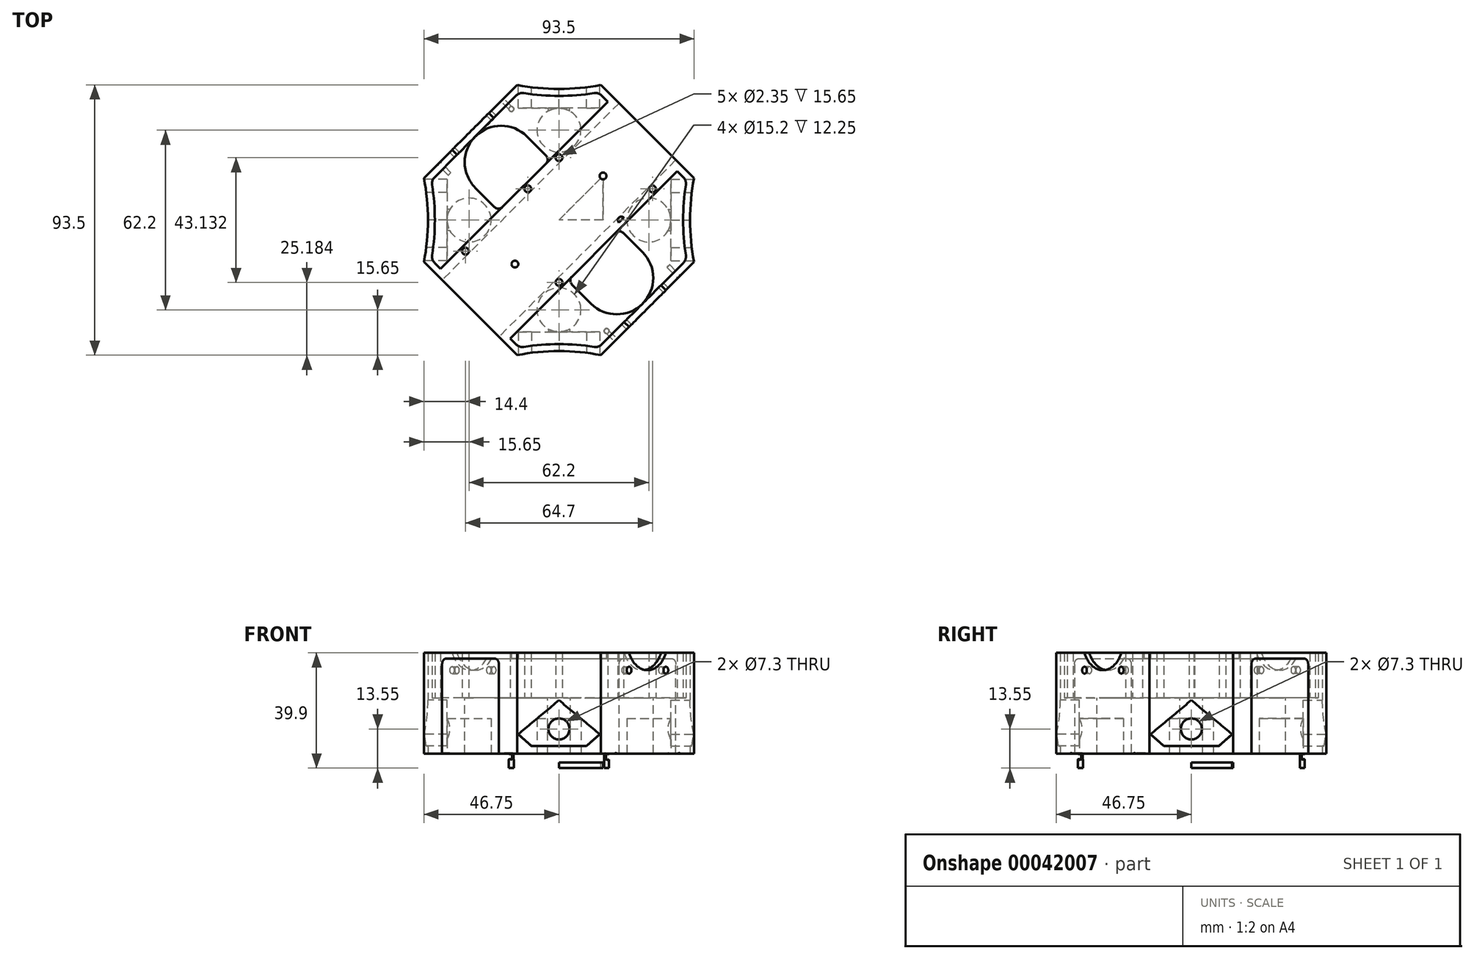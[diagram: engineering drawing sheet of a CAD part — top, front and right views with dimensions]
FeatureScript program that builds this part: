
annotation { "Feature Type Name" : "Feature", "Feature Type Description" : "" }
export const myFeature = defineFeature(function(context is Context, id is Id, definition is map)
    precondition{}
    {
        {
            var Q0;
            Q0=qCreatedBy(makeId("Top.planeOp"),FACE);
            var sketch = newSketch(context, id + "F0", { "sketchPlane" : qUnion([Q0])});
            skLineSegment(sketch, "E0", {"start": v(0, 0) * mm, "end": v(0, 46.75) * mm});
            skLineSegment(sketch, "E1", {"start": v(-14.5, 46.75) * mm, "end": v(14.5, 46.75) * mm});
            skLineSegment(sketch, "E2", {"start": v(0, 0) * mm, "end": v(46.75, 0) * mm});
            skLineSegment(sketch, "E3", {"start": v(46.75, 0) * mm, "end": v(0, 46.75) * mm});
            skLineSegment(sketch, "E4", {"start": v(0, 0) * mm, "end": v(23.37, 23.38) * mm});
            skLineSegment(sketch, "E5", {"start": v(46.75, 14.5) * mm, "end": v(46.75, -14.5) * mm});
            skLineSegment(sketch, "E6", {"start": v(14.5, 46.75) * mm, "end": v(46.75, 14.5) * mm});
            skLineSegment(sketch, "E7.MirrorCS", {"start": v(14.5, -46.75) * mm, "end": v(46.75, -14.5) * mm});
            skLineSegment(sketch, "E8.MirrorCS", {"start": v(46.75, 0) * mm, "end": v(0, -46.75) * mm});
            skLineSegment(sketch, "E9.MirrorCS", {"start": v(0, 0) * mm, "end": v(0, -46.75) * mm});
            skLineSegment(sketch, "E10.MirrorCS", {"start": v(0, 0) * mm, "end": v(23.37, -23.37) * mm});
            skLineSegment(sketch, "E11.MirrorCS", {"start": v(0, 0) * mm, "end": v(-23.37, -23.37) * mm});
            skLineSegment(sketch, "E12.MirrorCS", {"start": v(-46.75, 0) * mm, "end": v(0, -46.75) * mm});
            skLineSegment(sketch, "E13.MirrorCS", {"start": v(0, 0) * mm, "end": v(-23.37, 23.37) * mm});
            skLineSegment(sketch, "E14.MirrorCS", {"start": v(0, 0) * mm, "end": v(-46.75, 0) * mm});
            skLineSegment(sketch, "E15.MirrorCS", {"start": v(-14.5, -46.75) * mm, "end": v(-46.75, -14.5) * mm});
            skLineSegment(sketch, "E16.MirrorCS", {"start": v(-14.5, 46.75) * mm, "end": v(-46.75, 14.5) * mm});
            skLineSegment(sketch, "E17.MirrorCS", {"start": v(-46.75, 0) * mm, "end": v(0, 46.75) * mm});
            skLineSegment(sketch, "E18.MirrorCS", {"start": v(-46.75, 14.5) * mm, "end": v(-46.75, -14.5) * mm});
            skLineSegment(sketch, "E19", {"start": v(-14.5, -46.75) * mm, "end": v(14.5, -46.75) * mm});
            skSolve(sketch);
        }
        {
            var Q0;
            {var subQ1=sQuery(id+"F0.wireOp",EDGE,"E16.MirrorCS");Q0=makeQuery(id+"F0.imprint","IMPRINT",FACE,{"disambiguationData":[TD([[makeQuery(id+"F0.imprint","IMPRINT",EDGE,{"derivedFrom":subQ1}),1.0]])]});}
            var Q1;
            {var subQ0=sQuery(id+"F0.wireOp",EDGE,"E6");Q1=makeQuery(id+"F0.imprint","IMPRINT",FACE,{"disambiguationData":[TD([[makeQuery(id+"F0.imprint","IMPRINT",EDGE,{"derivedFrom":subQ0}),-1.0]])]});}
            var Q2;
            {var subQ1=sQuery(id+"F0.wireOp",EDGE,"E4");Q2=makeQuery(id+"F0.imprint","IMPRINT",FACE,{"disambiguationData":[TD([[makeQuery(id+"F0.imprint","IMPRINT",EDGE,{"derivedFrom":subQ1}),1.0]])]});}
            var Q3;
            {var subQ2=sQuery(id+"F0.wireOp",EDGE,"E0");Q3=makeQuery(id+"F0.imprint","IMPRINT",FACE,{"disambiguationData":[TD([[makeQuery(id+"F0.imprint","IMPRINT",EDGE,{"derivedFrom":subQ2}),1.0]])]});}
            var Q4;
            {var subQ1=sQuery(id+"F0.wireOp",EDGE,"E13.MirrorCS");Q4=makeQuery(id+"F0.imprint","IMPRINT",FACE,{"disambiguationData":[TD([[makeQuery(id+"F0.imprint","IMPRINT",EDGE,{"derivedFrom":subQ1}),1.0]])]});}
            var Q5;
            {var subQ2=sQuery(id+"F0.wireOp",EDGE,"E11.MirrorCS");Q5=makeQuery(id+"F0.imprint","IMPRINT",FACE,{"disambiguationData":[TD([[makeQuery(id+"F0.imprint","IMPRINT",EDGE,{"derivedFrom":subQ2}),-1.0]])]});}
            var Q6;
            {var subQ1=sQuery(id+"F0.wireOp",EDGE,"E15.MirrorCS");Q6=makeQuery(id+"F0.imprint","IMPRINT",FACE,{"disambiguationData":[TD([[makeQuery(id+"F0.imprint","IMPRINT",EDGE,{"derivedFrom":subQ1}),-1.0]])]});}
            var Q7;
            {var subQ2=sQuery(id+"F0.wireOp",EDGE,"E9.MirrorCS");Q7=makeQuery(id+"F0.imprint","IMPRINT",FACE,{"disambiguationData":[TD([[makeQuery(id+"F0.imprint","IMPRINT",EDGE,{"derivedFrom":subQ2}),-1.0]])]});}
            var Q8;
            {var subQ1=sQuery(id+"F0.wireOp",EDGE,"E9.MirrorCS");Q8=makeQuery(id+"F0.imprint","IMPRINT",FACE,{"disambiguationData":[TD([[makeQuery(id+"F0.imprint","IMPRINT",EDGE,{"derivedFrom":subQ1}),1.0]])]});}
            var Q9;
            {var subQ3=sQuery(id+"F0.wireOp",EDGE,"E7.MirrorCS");Q9=makeQuery(id+"F0.imprint","IMPRINT",FACE,{"disambiguationData":[TD([[makeQuery(id+"F0.imprint","IMPRINT",EDGE,{"derivedFrom":subQ3}),1.0]])]});}
            var Q10;
            {var subQ2=sQuery(id+"F0.wireOp",EDGE,"E2");Q10=makeQuery(id+"F0.imprint","IMPRINT",FACE,{"disambiguationData":[TD([[makeQuery(id+"F0.imprint","IMPRINT",EDGE,{"derivedFrom":subQ2}),-1.0]])]});}
            var Q11;
            {var subQ2=sQuery(id+"F0.wireOp",EDGE,"E2");Q11=makeQuery(id+"F0.imprint","IMPRINT",FACE,{"disambiguationData":[TD([[makeQuery(id+"F0.imprint","IMPRINT",EDGE,{"derivedFrom":subQ2}),1.0]])]});}
            extrude(context, id + "F1", {"entities" : qUnion([Q0, Q1, Q2, Q3, Q4, Q5, Q6, Q7, Q8, Q9, Q10, Q11]), "depth" : 24.25 * mm});
        }
        {
            var Q0;
            Q0=makeQuery(id+"F1.opExtrude","SWEPT_FACE",FACE,{"disambiguationData":[OSD([sQuery(id+"F0.wireOp",EDGE,"E19")])]});
            var sketch = newSketch(context, id + "F2", { "sketchPlane" : qUnion([Q0])});
            skLineSegment(sketch, "E20", {"start": v(9.5, 7.65) * mm, "end": v(14.1, 11.7) * mm});
            skLineSegment(sketch, "E21", {"start": v(0, 11.7) * mm, "end": v(0, 7.65) * mm});
            skLineSegment(sketch, "E22.MirrorCS", {"start": v(0, 11.7) * mm, "end": v(-14.1, 11.7) * mm});
            skPoint(sketch, "E23.endSnap0", {"position": v(0, 24.25) * mm});
            skLineSegment(sketch, "E24.MirrorCS", {"start": v(-9.5, 7.65) * mm, "end": v(-14.1, 11.7) * mm});
            skLineSegment(sketch, "E25.MirrorCS", {"start": v(0, 7.65) * mm, "end": v(-9.5, 7.65) * mm});
            skLineSegment(sketch, "E26", {"start": v(-14.1, 11.7) * mm, "end": v(0, 23.5) * mm});
            skLineSegment(sketch, "E27", {"start": v(14.1, 11.7) * mm, "end": v(0, 23.5) * mm});
            skLineSegment(sketch, "E28", {"start": v(0, 11.7) * mm, "end": v(14.1, 11.7) * mm});
            skLineSegment(sketch, "E29", {"start": v(0, 7.65) * mm, "end": v(9.5, 7.65) * mm});
            skLineSegment(sketch, "E30", {"start": v(0, 23.5) * mm, "end": v(0, 11.7) * mm});
            skLineSegment(sketch, "E23", {"start": v(0, 24.25) * mm, "end": v(0, 23.5) * mm});
            skSolve(sketch);
        }
        {
            var Q0;
            Q0 = qSketchRegion(id + "F2", true);
            extrude(context, id + "F3", {"entities" : qUnion([Q0]), "operationType" : NewBodyOperationType.REMOVE, "oppositeDirection" : true, "depth" : 8 * mm});
        }
        {
            var Q0;
            Q0=makeQuery(id+"F1.opExtrude","SWEPT_FACE",FACE,{"disambiguationData":[OSD([sQuery(id+"F0.wireOp",EDGE,"E5")])]});
            var sketch = newSketch(context, id + "F4", { "sketchPlane" : qUnion([Q0])});
            skLineSegment(sketch, "E31", {"start": v(-98.22, 44.38) * mm, "end": v(-93.52, 48.48) * mm});
            skLineSegment(sketch, "E32", {"start": v(-107.72, 48.48) * mm, "end": v(-107.72, 44.38) * mm});
            skLineSegment(sketch, "E33.MirrorCS", {"start": v(-107.72, 48.48) * mm, "end": v(-121.92, 48.48) * mm});
            skPoint(sketch, "E34.endSnap0", {"position": v(-107.72, 61.13) * mm});
            skLineSegment(sketch, "E35.MirrorCS", {"start": v(-117.22, 44.38) * mm, "end": v(-121.92, 48.48) * mm});
            skLineSegment(sketch, "E36.MirrorCS", {"start": v(-107.72, 44.38) * mm, "end": v(-117.22, 44.38) * mm});
            skLineSegment(sketch, "E37", {"start": v(-121.92, 48.48) * mm, "end": v(-107.72, 60.38) * mm});
            skLineSegment(sketch, "E38", {"start": v(-93.52, 48.48) * mm, "end": v(-107.72, 60.38) * mm});
            skLineSegment(sketch, "E39", {"start": v(-107.72, 48.48) * mm, "end": v(-93.52, 48.48) * mm});
            skLineSegment(sketch, "E40", {"start": v(-107.72, 44.38) * mm, "end": v(-98.22, 44.38) * mm});
            skLineSegment(sketch, "E41", {"start": v(-107.72, 60.38) * mm, "end": v(-107.72, 48.48) * mm});
            skLineSegment(sketch, "E34", {"start": v(-107.72, 61.13) * mm, "end": v(-107.72, 60.38) * mm});
            skLineSegment(sketch, "E42", {"start": v(9.5, 7.65) * mm, "end": v(14.1, 11.7) * mm});
            skLineSegment(sketch, "E43", {"start": v(0, 11.7) * mm, "end": v(0, 7.65) * mm});
            skLineSegment(sketch, "E44.MirrorCS", {"start": v(0, 11.7) * mm, "end": v(-14.1, 11.7) * mm});
            skPoint(sketch, "E45.endSnap0", {"position": v(0, 24.25) * mm});
            skLineSegment(sketch, "E46.MirrorCS", {"start": v(-9.5, 7.65) * mm, "end": v(-14.1, 11.7) * mm});
            skLineSegment(sketch, "E47.MirrorCS", {"start": v(0, 7.65) * mm, "end": v(-9.5, 7.65) * mm});
            skLineSegment(sketch, "E48", {"start": v(-14.1, 11.7) * mm, "end": v(0, 23.5) * mm});
            skLineSegment(sketch, "E49", {"start": v(14.1, 11.7) * mm, "end": v(0, 23.5) * mm});
            skLineSegment(sketch, "E50", {"start": v(0, 11.7) * mm, "end": v(14.1, 11.7) * mm});
            skLineSegment(sketch, "E51", {"start": v(0, 7.65) * mm, "end": v(9.5, 7.65) * mm});
            skLineSegment(sketch, "E52", {"start": v(0, 23.5) * mm, "end": v(0, 11.7) * mm});
            skLineSegment(sketch, "E45", {"start": v(0, 24.25) * mm, "end": v(0, 23.5) * mm});
            skSolve(sketch);
        }
        {
            var Q0;
            Q0 = qSketchRegion(id + "F4", true);
            extrude(context, id + "F5", {"entities" : qUnion([Q0]), "operationType" : NewBodyOperationType.REMOVE, "oppositeDirection" : true, "depth" : 8 * mm});
        }
        {
            var Q0;
            Q0=makeQuery(id+"F1.opExtrude","SWEPT_FACE",FACE,{"disambiguationData":[OSD([sQuery(id+"F0.wireOp",EDGE,"E1")])]});
            var sketch = newSketch(context, id + "F6", { "sketchPlane" : qUnion([Q0])});
            skLineSegment(sketch, "E53", {"start": v(9.5, 7.65) * mm, "end": v(14.1, 11.7) * mm});
            skLineSegment(sketch, "E54", {"start": v(0, 11.7) * mm, "end": v(0, 7.65) * mm});
            skLineSegment(sketch, "E55.MirrorCS", {"start": v(0, 11.7) * mm, "end": v(-14.1, 11.7) * mm});
            skPoint(sketch, "E56.endSnap0", {"position": v(0, 24.25) * mm});
            skLineSegment(sketch, "E57.MirrorCS", {"start": v(-9.5, 7.65) * mm, "end": v(-14.1, 11.7) * mm});
            skLineSegment(sketch, "E58.MirrorCS", {"start": v(0, 7.65) * mm, "end": v(-9.5, 7.65) * mm});
            skLineSegment(sketch, "E59", {"start": v(-14.1, 11.7) * mm, "end": v(0, 23.5) * mm});
            skLineSegment(sketch, "E60", {"start": v(14.1, 11.7) * mm, "end": v(0, 23.5) * mm});
            skLineSegment(sketch, "E61", {"start": v(0, 11.7) * mm, "end": v(14.1, 11.7) * mm});
            skLineSegment(sketch, "E62", {"start": v(0, 7.65) * mm, "end": v(9.5, 7.65) * mm});
            skLineSegment(sketch, "E63", {"start": v(0, 23.5) * mm, "end": v(0, 11.7) * mm});
            skLineSegment(sketch, "E56", {"start": v(0, 24.25) * mm, "end": v(0, 23.5) * mm});
            skSolve(sketch);
        }
        {
            var Q0;
            Q0 = qSketchRegion(id + "F6", true);
            extrude(context, id + "F7", {"entities" : qUnion([Q0]), "operationType" : NewBodyOperationType.REMOVE, "oppositeDirection" : true, "depth" : 8 * mm});
        }
        {
            var Q0;
            Q0=makeQuery(id+"F1.opExtrude","SWEPT_FACE",FACE,{"disambiguationData":[OSD([sQuery(id+"F0.wireOp",EDGE,"E18.MirrorCS")])]});
            var sketch = newSketch(context, id + "F8", { "sketchPlane" : qUnion([Q0])});
            skLineSegment(sketch, "E64", {"start": v(9.5, 7.65) * mm, "end": v(14.1, 11.7) * mm});
            skLineSegment(sketch, "E65", {"start": v(0, 11.7) * mm, "end": v(0, 7.65) * mm});
            skLineSegment(sketch, "E66.MirrorCS", {"start": v(0, 11.7) * mm, "end": v(-14.1, 11.7) * mm});
            skPoint(sketch, "E67.endSnap0", {"position": v(0, 24.25) * mm});
            skLineSegment(sketch, "E68.MirrorCS", {"start": v(-9.5, 7.65) * mm, "end": v(-14.1, 11.7) * mm});
            skLineSegment(sketch, "E69.MirrorCS", {"start": v(0, 7.65) * mm, "end": v(-9.5, 7.65) * mm});
            skLineSegment(sketch, "E70", {"start": v(-14.1, 11.7) * mm, "end": v(0, 23.5) * mm});
            skLineSegment(sketch, "E71", {"start": v(14.1, 11.7) * mm, "end": v(0, 23.5) * mm});
            skLineSegment(sketch, "E72", {"start": v(0, 11.7) * mm, "end": v(14.1, 11.7) * mm});
            skLineSegment(sketch, "E73", {"start": v(0, 7.65) * mm, "end": v(9.5, 7.65) * mm});
            skLineSegment(sketch, "E74", {"start": v(0, 23.5) * mm, "end": v(0, 11.7) * mm});
            skLineSegment(sketch, "E67", {"start": v(0, 24.25) * mm, "end": v(0, 23.5) * mm});
            skSolve(sketch);
        }
        {
            var Q0;
            Q0 = qSketchRegion(id + "F8", true);
            extrude(context, id + "F9", {"entities" : qUnion([Q0]), "operationType" : NewBodyOperationType.REMOVE, "oppositeDirection" : true, "depth" : 8 * mm});
        }
        {
            var Q0;
            Q0=qCreatedBy(makeId("Top.planeOp"),FACE);
            var sketch = newSketch(context, id + "F10", { "sketchPlane" : qUnion([Q0])});
            skLineSegment(sketch, "E75", {"start": v(0, 0) * mm, "end": v(0, -121.56) * mm});
            skCircle(sketch, "E76", {"center": v(0, -121.56) * mm, "radius": 76.2 * mm});
            skLineSegment(sketch, "E77.MirrorCS", {"start": v(0, 0) * mm, "end": v(0, 121.56) * mm});
            skCircle(sketch, "E78.MirrorC", {"center": v(0, 121.56) * mm, "radius": 76.2 * mm});
            skLineSegment(sketch, "E79", {"start": v(0, 0) * mm, "end": v(-30.62, -30.63) * mm});
            skCircle(sketch, "E80.MirrorC", {"center": v(-121.56, 0) * mm, "radius": 76.2 * mm});
            skLineSegment(sketch, "E81.MirrorCS", {"start": v(0, 0) * mm, "end": v(121.56, 0) * mm});
            skCircle(sketch, "E82.MirrorC", {"center": v(121.56, 0) * mm, "radius": 76.2 * mm});
            skLineSegment(sketch, "E83.MirrorCS", {"start": v(0, 0) * mm, "end": v(-121.56, 0) * mm});
            skSolve(sketch);
        }
        {
            var Q0;
            Q0 = qSketchRegion(id + "F10", true);
            var Q1;
            {var subQ0=sQuery(id+"F10.wireOp",EDGE,"93edd87a-cf2b-4698-b4c2-4d48644ee807");var subQ3=sQuery(id+"F10.wireOp",EDGE,"E77.MirrorCS");var subQ4=makeQuery(id+"F10.imprint","INTERSECT",VERTEX,{"derivedFrom":[subQ3,subQ0]});Q1=makeQuery(id+"F10.imprint","IMPRINT",FACE,{"disambiguationData":[TD([[makeQuery(id+"F10.imprint","IMPRINT",EDGE,{"disambiguationData":[TD([[subQ4,1.0]])],"derivedFrom":subQ0}),1.0]])]});}
            var Q2;
            {var subQ0=sQuery(id+"F10.wireOp",EDGE,"93edd87a-cf2b-4698-b4c2-4d48644ee807");var subQ3=sQuery(id+"F10.wireOp",EDGE,"E77.MirrorCS");var subQ4=makeQuery(id+"F10.imprint","INTERSECT",VERTEX,{"derivedFrom":[subQ3,subQ0]});Q2=makeQuery(id+"F10.imprint","IMPRINT",FACE,{"disambiguationData":[TD([[makeQuery(id+"F10.imprint","IMPRINT",EDGE,{"disambiguationData":[TD([[subQ4,-1.0]])],"derivedFrom":subQ0}),1.0]])]});}
            var Q3;
            {var subQ0=sQuery(id+"F10.wireOp",EDGE,"93edd87a-cf2b-4698-b4c2-4d48644ee807");var subQ3=sQuery(id+"F10.wireOp",EDGE,"E75");var subQ4=makeQuery(id+"F10.imprint","INTERSECT",VERTEX,{"derivedFrom":[subQ3,subQ0]});Q3=makeQuery(id+"F10.imprint","IMPRINT",FACE,{"disambiguationData":[TD([[makeQuery(id+"F10.imprint","IMPRINT",EDGE,{"disambiguationData":[TD([[subQ4,-1.0]])],"derivedFrom":subQ0}),1.0]])]});}
            var Q4;
            {var subQ0=sQuery(id+"F10.wireOp",EDGE,"E79");var subQ1=sQuery(id+"F10.wireOp",EDGE,"93edd87a-cf2b-4698-b4c2-4d48644ee807");var subQ2=makeQuery(id+"F10.imprint","INTERSECT",VERTEX,{"derivedFrom":[subQ0,subQ1]});Q4=makeQuery(id+"F10.imprint","IMPRINT",FACE,{"disambiguationData":[TD([[makeQuery(id+"F10.imprint","IMPRINT",EDGE,{"disambiguationData":[TD([[subQ2,-1.0]])],"derivedFrom":subQ1}),1.0]])]});}
            var Q5;
            {var subQ0=sQuery(id+"F10.wireOp",EDGE,"93edd87a-cf2b-4698-b4c2-4d48644ee807");var subQ3=sQuery(id+"F10.wireOp",EDGE,"E79");var subQ4=makeQuery(id+"F10.imprint","INTERSECT",VERTEX,{"derivedFrom":[subQ3,subQ0]});Q5=makeQuery(id+"F10.imprint","IMPRINT",FACE,{"disambiguationData":[TD([[makeQuery(id+"F10.imprint","IMPRINT",EDGE,{"disambiguationData":[TD([[subQ4,1.0]])],"derivedFrom":subQ0}),1.0]])]});}
            extrude(context, id + "F11", {"entities" : qUnion([Q0, Q1, Q2, Q3, Q4, Q5]), "operationType" : NewBodyOperationType.REMOVE, "depth" : 45 * mm});
        }
        {
            var Q0;
            Q0=qCreatedBy(makeId("Top.planeOp"),FACE);
            cPlane(context, id + "F12", {"entities" : qUnion([Q0]), "cplaneType" : CPlaneType.OFFSET, "offset" : 5.35 * mm, "width" : 150 * mm, "height" : 150 * mm});
        }
        {
            var Q0;
            Q0=makeQuery(id+"F1.opExtrude","CAP_FACE",FACE,{"disambiguationData":[OSD([sQuery(id+"F0.wireOp",EDGE,"E1"),sQuery(id+"F0.wireOp",EDGE,"E5"),sQuery(id+"F0.wireOp",EDGE,"E6"),sQuery(id+"F0.wireOp",EDGE,"E7.MirrorCS"),sQuery(id+"F0.wireOp",EDGE,"E15.MirrorCS"),sQuery(id+"F0.wireOp",EDGE,"E16.MirrorCS"),sQuery(id+"F0.wireOp",EDGE,"E18.MirrorCS"),sQuery(id+"F0.wireOp",EDGE,"E19")])],"isStart":true});
            var sketch = newSketch(context, id + "F13", { "sketchPlane" : qUnion([Q0])});
            skLineSegment(sketch, "E84", {"start": v(0, 0) * mm, "end": v(23, -23) * mm});
            skLineSegment(sketch, "E85.MirrorCS", {"start": v(0, 0) * mm, "end": v(-23, -23) * mm});
            skCircle(sketch, "E86.MirrorC", {"center": v(0, -31.1) * mm, "radius": 7.6 * mm});
            skCircle(sketch, "E87.MirrorC", {"center": v(-31.1, 0) * mm, "radius": 7.6 * mm});
            skCircle(sketch, "E88.MirrorC", {"center": v(31.1, 0) * mm, "radius": 7.6 * mm});
            skCircle(sketch, "E89", {"center": v(0, 31.1) * mm, "radius": 7.6 * mm});
            skLineSegment(sketch, "E90.MirrorCS", {"start": v(0, 0) * mm, "end": v(-31.1, 0) * mm});
            skLineSegment(sketch, "E91", {"start": v(0, 0) * mm, "end": v(0, 31.1) * mm});
            skLineSegment(sketch, "E92.MirrorCS", {"start": v(0, 0) * mm, "end": v(0, -31.1) * mm});
            skLineSegment(sketch, "E93", {"start": v(0, 0) * mm, "end": v(23, 23) * mm});
            skLineSegment(sketch, "E94.MirrorCS", {"start": v(0, 0) * mm, "end": v(31.1, 0) * mm});
            skSolve(sketch);
        }
        {
            var Q0;
            Q0=qSketchRegion(id+"F13",true);
            extrude(context, id + "F14", {"entities" : qUnion([Q0]), "operationType" : NewBodyOperationType.REMOVE, "oppositeDirection" : true, "depth" : 17.25 * mm});
        }
        {
            var Q0;
            Q0=makeQuery(id+"F1.opExtrude","CAP_FACE",FACE,{"disambiguationData":[OSD([sQuery(id+"F0.wireOp",EDGE,"E1"),sQuery(id+"F0.wireOp",EDGE,"E5"),sQuery(id+"F0.wireOp",EDGE,"E6"),sQuery(id+"F0.wireOp",EDGE,"E7.MirrorCS"),sQuery(id+"F0.wireOp",EDGE,"E15.MirrorCS"),sQuery(id+"F0.wireOp",EDGE,"E16.MirrorCS"),sQuery(id+"F0.wireOp",EDGE,"E18.MirrorCS"),sQuery(id+"F0.wireOp",EDGE,"E19")])],"isStart":false});
            var sketch = newSketch(context, id + "F15", { "sketchPlane" : qUnion([Q0])});
            skLineSegment(sketch, "E95.MirrorCS", {"start": v(0, 0) * mm, "end": v(121.56, 0) * mm});
            skArc(sketch, "E96.MirrorC", {"start": v(46.75, 14.5) * mm, "mid": v(45.36, 0) * mm, "end": v(46.75, -14.5) * mm});
            skArc(sketch, "E97.MirrorC", {"start": v(-46.75, 14.5) * mm, "mid": v(-45.36, 0) * mm, "end": v(-46.75, -14.5) * mm});
            skLineSegment(sketch, "E98", {"start": v(0, 0) * mm, "end": v(0, 121.56) * mm});
            skArc(sketch, "E99", {"start": v(-14.5, 46.75) * mm, "mid": v(0, 45.36) * mm, "end": v(14.5, 46.75) * mm});
            skArc(sketch, "E100.MirrorC", {"start": v(-14.5, -46.75) * mm, "mid": v(0, -45.36) * mm, "end": v(14.5, -46.75) * mm});
            skLineSegment(sketch, "E101", {"start": v(-14.5, 46.75) * mm, "end": v(-14.5, 46.75) * mm});
            skLineSegment(sketch, "E102", {"start": v(14.5, 46.75) * mm, "end": v(46.75, 14.5) * mm});
            skLineSegment(sketch, "E103", {"start": v(46.75, 14.5) * mm, "end": v(46.75, 14.5) * mm});
            skLineSegment(sketch, "E104", {"start": v(46.75, -14.5) * mm, "end": v(14.5, -46.75) * mm});
            skLineSegment(sketch, "E105", {"start": v(14.5, -46.75) * mm, "end": v(14.5, -46.75) * mm});
            skLineSegment(sketch, "E106.trimOffspring", {"start": v(14.5, 46.75) * mm, "end": v(14.5, 46.75) * mm});
            skLineSegment(sketch, "E107.trimOffspring", {"start": v(46.75, -14.5) * mm, "end": v(46.75, -14.5) * mm});
            skLineSegment(sketch, "E108.trimOffspring", {"start": v(-14.5, -46.75) * mm, "end": v(-14.5, -46.75) * mm});
            skLineSegment(sketch, "E109", {"start": v(0, 0) * mm, "end": v(-121.56, 0) * mm});
            skLineSegment(sketch, "E110", {"start": v(-14.5, 46.75) * mm, "end": v(-46.75, 14.5) * mm});
            skLineSegment(sketch, "E111", {"start": v(-46.75, 14.5) * mm, "end": v(-46.75, 14.5) * mm});
            skLineSegment(sketch, "E112", {"start": v(-46.75, -14.5) * mm, "end": v(-14.5, -46.75) * mm});
            skLineSegment(sketch, "E113.trimOffspring", {"start": v(-46.75, -14.5) * mm, "end": v(-46.75, -14.5) * mm});
            skArc(sketch, "E114.0", {"start": v(-12.2, 43.91) * mm, "mid": v(0, 42.96) * mm, "end": v(12.2, 43.91) * mm});
            skLineSegment(sketch, "E114.1", {"start": v(14.79, 43.07) * mm, "end": v(43.07, 14.79) * mm});
            skLineSegment(sketch, "E114.2", {"start": v(-14.79, 43.07) * mm, "end": v(-43.07, 14.79) * mm});
            skArc(sketch, "E114.3", {"start": v(43.91, 12.2) * mm, "mid": v(42.96, 0) * mm, "end": v(43.91, -12.2) * mm});
            skArc(sketch, "E114.4", {"start": v(-43.91, 12.2) * mm, "mid": v(-42.96, 0) * mm, "end": v(-43.91, -12.2) * mm});
            skLineSegment(sketch, "E114.5", {"start": v(-43.07, -14.79) * mm, "end": v(-14.79, -43.07) * mm});
            skArc(sketch, "E114.6", {"start": v(-12.2, -43.91) * mm, "mid": v(0, -42.96) * mm, "end": v(12.2, -43.91) * mm});
            skLineSegment(sketch, "E114.7", {"start": v(43.07, -14.79) * mm, "end": v(14.79, -43.07) * mm});
            skPoint(sketch, "E115.visualSharp", {"position": v(-44.16, -13.7) * mm});
            skArc(sketch, "E115.filletArc", {"start": v(-43.91, -12.2) * mm, "mid": v(-43.8, -13.6) * mm, "end": v(-43.07, -14.79) * mm});
            skPoint(sketch, "E116.visualSharp", {"position": v(-13.7, -44.16) * mm});
            skArc(sketch, "E116.filletArc", {"start": v(-14.79, -43.07) * mm, "mid": v(-13.6, -43.8) * mm, "end": v(-12.2, -43.91) * mm});
            skPoint(sketch, "E117.visualSharp", {"position": v(13.7, -44.16) * mm});
            skArc(sketch, "E117.filletArc", {"start": v(12.2, -43.91) * mm, "mid": v(13.6, -43.8) * mm, "end": v(14.79, -43.07) * mm});
            skPoint(sketch, "E118.visualSharp", {"position": v(44.16, -13.7) * mm});
            skArc(sketch, "E118.filletArc", {"start": v(43.07, -14.79) * mm, "mid": v(43.8, -13.6) * mm, "end": v(43.91, -12.2) * mm});
            skPoint(sketch, "E119.visualSharp", {"position": v(44.16, 13.7) * mm});
            skArc(sketch, "E119.filletArc", {"start": v(43.91, 12.2) * mm, "mid": v(43.8, 13.6) * mm, "end": v(43.07, 14.79) * mm});
            skPoint(sketch, "E120.visualSharp", {"position": v(13.7, 44.16) * mm});
            skArc(sketch, "E120.filletArc", {"start": v(14.79, 43.07) * mm, "mid": v(13.6, 43.8) * mm, "end": v(12.2, 43.91) * mm});
            skPoint(sketch, "E121.visualSharp", {"position": v(-44.16, 13.7) * mm});
            skArc(sketch, "E121.filletArc", {"start": v(-43.07, 14.79) * mm, "mid": v(-43.8, 13.6) * mm, "end": v(-43.91, 12.2) * mm});
            skPoint(sketch, "E122.visualSharp", {"position": v(-13.7, 44.16) * mm});
            skArc(sketch, "E122.filletArc", {"start": v(-12.2, 43.91) * mm, "mid": v(-13.6, 43.8) * mm, "end": v(-14.79, 43.07) * mm});
            skSolve(sketch);
        }
        {
            var Q0;
            Q0=makeQuery(id+"F15.imprint","IMPRINT",FACE,{"disambiguationData":[TD([[makeQuery(id+"F15.imprint","IMPRINT",EDGE,{"derivedFrom":sQuery(id+"F15.wireOp",EDGE,"38fca557-5818-491b-96ee-555abbfffb0f.0")}),1.0]])]});
            var Q1;
            Q1=makeQuery(id+"F15.imprint","IMPRINT",FACE,{"disambiguationData":[TD([[makeQuery(id+"F15.imprint","IMPRINT",EDGE,{"derivedFrom":sQuery(id+"F15.wireOp",EDGE,"38fca557-5818-491b-96ee-555abbfffb0f.1")}),1.0]])]});
            var Q2;
            Q2=makeQuery(id+"F15.imprint","IMPRINT",FACE,{"disambiguationData":[TD([[makeQuery(id+"F15.imprint","IMPRINT",EDGE,{"derivedFrom":sQuery(id+"F15.wireOp",EDGE,"d639dd6d-9a94-4636-acb7-059c743e6398.0")}),-1.0]])]});
            var Q3;
            Q3=makeQuery(id+"F15.imprint","IMPRINT",FACE,{"disambiguationData":[TD([[makeQuery(id+"F15.imprint","IMPRINT",EDGE,{"derivedFrom":sQuery(id+"F15.wireOp",EDGE,"d639dd6d-9a94-4636-acb7-059c743e6398.1")}),-1.0]])]});
            var Q4;
            {var subQ4=sQuery(id+"F15.wireOp",EDGE,"E102");Q4=makeQuery(id+"F15.imprint","IMPRINT",FACE,{"disambiguationData":[TD([[makeQuery(id+"F15.imprint","IMPRINT",EDGE,{"derivedFrom":subQ4}),-1.0]])]});}
            var Q5;
            {var subQ7=sQuery(id+"F15.wireOp",EDGE,"E114.2");Q5=makeQuery(id+"F15.imprint","IMPRINT",FACE,{"disambiguationData":[TD([[makeQuery(id+"F15.imprint","IMPRINT",EDGE,{"derivedFrom":subQ7}),-1.0]])]});}
            var Q6;
            {var subQ0=sQuery(id+"F15.wireOp",EDGE,"E104");Q6=makeQuery(id+"F15.imprint","IMPRINT",FACE,{"disambiguationData":[TD([[makeQuery(id+"F15.imprint","IMPRINT",EDGE,{"derivedFrom":subQ0}),1.0]])]});}
            var Q7;
            {var subQ1=sQuery(id+"F0.wireOp",EDGE,"E16.MirrorCS");var subQ3=makeQuery(id+"F1.opExtrude","CAP_EDGE",EDGE,{"disambiguationData":[OSD([subQ1])],"isStart":false});Q7=makeQuery(id+"F15.imprint","IMPRINT",FACE,{"disambiguationData":[TD([[makeQuery(id+"F15.imprint","IMPRINT",EDGE,{"derivedFrom":subQ3}),1.0]])]});}
            var Q8;
            {var subQ1=sQuery(id+"F0.wireOp",EDGE,"E15.MirrorCS");var subQ3=makeQuery(id+"F1.opExtrude","CAP_EDGE",EDGE,{"disambiguationData":[OSD([subQ1])],"isStart":false});Q8=makeQuery(id+"F15.imprint","IMPRINT",FACE,{"disambiguationData":[TD([[makeQuery(id+"F15.imprint","IMPRINT",EDGE,{"derivedFrom":subQ3}),-1.0]])]});}
            extrude(context, id + "F16", {"entities" : qUnion([Q0, Q1, Q2, Q3, Q4, Q5, Q6, Q7, Q8]), "operationType" : NewBodyOperationType.ADD, "depth" : 15.65 * mm});
        }
        {
            var Q0;
            Q0=makeQuery(id+"F3.boolean.opBoolean","COPY",FACE,{"derivedFrom":makeQuery(id+"F3.opExtrude","CAP_FACE",FACE,{"disambiguationData":[OSD([sQuery(id+"F2.wireOp",EDGE,"E20"),sQuery(id+"F2.wireOp",EDGE,"E24.MirrorCS"),sQuery(id+"F2.wireOp",EDGE,"E25.MirrorCS"),sQuery(id+"F2.wireOp",EDGE,"E26"),sQuery(id+"F2.wireOp",EDGE,"E27"),sQuery(id+"F2.wireOp",EDGE,"E29")])],"isStart":false})});
            var sketch = newSketch(context, id + "F17", { "sketchPlane" : qUnion([Q0])});
            skLineSegment(sketch, "E123", {"start": v(0, 13.55) * mm, "end": v(0, 7.65) * mm});
            skCircle(sketch, "E124", {"center": v(0, 13.55) * mm, "radius": 3.65 * mm});
            skSolve(sketch);
        }
        {
            var Q0;
            Q0 = qSketchRegion(id + "F17", true);
            extrude(context, id + "F18", {"entities" : qUnion([Q0]), "operationType" : NewBodyOperationType.REMOVE, "oppositeDirection" : true, "depth" : 5 * mm});
        }
        {
            var Q0;
            Q0=makeQuery(id+"F5.boolean.opBoolean","COPY",FACE,{"derivedFrom":makeQuery(id+"F5.opExtrude","CAP_FACE",FACE,{"disambiguationData":[OSD([sQuery(id+"F4.wireOp",EDGE,"E42"),sQuery(id+"F4.wireOp",EDGE,"E46.MirrorCS"),sQuery(id+"F4.wireOp",EDGE,"E47.MirrorCS"),sQuery(id+"F4.wireOp",EDGE,"E48"),sQuery(id+"F4.wireOp",EDGE,"E49"),sQuery(id+"F4.wireOp",EDGE,"E51")])],"isStart":false})});
            var sketch = newSketch(context, id + "F19", { "sketchPlane" : qUnion([Q0])});
            skLineSegment(sketch, "E125", {"start": v(0, 13.55) * mm, "end": v(0, 7.65) * mm});
            skCircle(sketch, "E126", {"center": v(0, 13.55) * mm, "radius": 3.65 * mm});
            skSolve(sketch);
        }
        {
            var Q0;
            Q0 = qSketchRegion(id + "F19", true);
            extrude(context, id + "F20", {"entities" : qUnion([Q0]), "operationType" : NewBodyOperationType.REMOVE, "oppositeDirection" : true, "depth" : 5 * mm});
        }
        {
            var Q0;
            Q0=makeQuery(id+"F7.boolean.opBoolean","COPY",FACE,{"derivedFrom":makeQuery(id+"F7.opExtrude","CAP_FACE",FACE,{"disambiguationData":[OSD([sQuery(id+"F6.wireOp",EDGE,"E53"),sQuery(id+"F6.wireOp",EDGE,"E57.MirrorCS"),sQuery(id+"F6.wireOp",EDGE,"E58.MirrorCS"),sQuery(id+"F6.wireOp",EDGE,"E59"),sQuery(id+"F6.wireOp",EDGE,"E60"),sQuery(id+"F6.wireOp",EDGE,"E62")])],"isStart":false})});
            var sketch = newSketch(context, id + "F21", { "sketchPlane" : qUnion([Q0])});
            skLineSegment(sketch, "E127", {"start": v(0, 13.55) * mm, "end": v(0, 7.65) * mm});
            skCircle(sketch, "E128", {"center": v(0, 13.55) * mm, "radius": 3.65 * mm});
            skSolve(sketch);
        }
        {
            var Q0;
            Q0=makeQuery(id+"F9.boolean.opBoolean","COPY",FACE,{"derivedFrom":makeQuery(id+"F9.opExtrude","CAP_FACE",FACE,{"disambiguationData":[OSD([sQuery(id+"F8.wireOp",EDGE,"E64"),sQuery(id+"F8.wireOp",EDGE,"E68.MirrorCS"),sQuery(id+"F8.wireOp",EDGE,"E69.MirrorCS"),sQuery(id+"F8.wireOp",EDGE,"E70"),sQuery(id+"F8.wireOp",EDGE,"E71"),sQuery(id+"F8.wireOp",EDGE,"E73")])],"isStart":false})});
            var sketch = newSketch(context, id + "F22", { "sketchPlane" : qUnion([Q0])});
            skLineSegment(sketch, "E129", {"start": v(0, 13.55) * mm, "end": v(0, 7.65) * mm});
            skCircle(sketch, "E130", {"center": v(0, 13.55) * mm, "radius": 3.65 * mm});
            skSolve(sketch);
        }
        {
            var Q0;
            Q0 = qSketchRegion(id + "F21", true);
            extrude(context, id + "F23", {"entities" : qUnion([Q0]), "operationType" : NewBodyOperationType.REMOVE, "oppositeDirection" : true, "depth" : 1.7 * mm});
        }
        {
            var Q0;
            Q0 = qSketchRegion(id + "F22", true);
            extrude(context, id + "F24", {"entities" : qUnion([Q0]), "operationType" : NewBodyOperationType.REMOVE, "oppositeDirection" : true, "depth" : 1.7 * mm});
        }
        {
            var Q0;
            Q0=makeQuery(id+"F16.boolean.opBoolean","MERGE",FACE,{"derivedFrom":[makeQuery(id+"F1.opExtrude","SWEPT_FACE",FACE,{"disambiguationData":[OSD([sQuery(id+"F0.wireOp",EDGE,"E6")])]}),makeQuery(id+"F16.opExtrude","SWEPT_FACE",FACE,{"disambiguationData":[OSD([sQuery(id+"F15.wireOp",EDGE,"72493947-4794-4d5b-8e6e-f786664ce59e.4")])]})]});
            var sketch = newSketch(context, id + "F25", { "sketchPlane" : qUnion([Q0])});
            skLineSegment(sketch, "E131", {"start": v(0, 0) * mm, "end": v(0, 25) * mm});
            skPoint(sketch, "E131.endSnap0", {"position": v(0, 0) * mm});
            skLineSegment(sketch, "E132", {"start": v(0, 25) * mm, "end": v(13, 25) * mm});
            skCircle(sketch, "E133", {"center": v(13, 25) * mm, "radius": 1.5 * mm});
            skLineSegment(sketch, "E134.MirrorCS", {"start": v(0, 25) * mm, "end": v(-13, 25) * mm});
            skCircle(sketch, "E135.MirrorC", {"center": v(-13, 25) * mm, "radius": 1.5 * mm});
            skSolve(sketch);
        }
        {
            var Q0;
            Q0=makeQuery(id+"F16.boolean.opBoolean","MERGE",FACE,{"derivedFrom":[makeQuery(id+"F1.opExtrude","SWEPT_FACE",FACE,{"disambiguationData":[OSD([sQuery(id+"F0.wireOp",EDGE,"E15.MirrorCS")])]}),makeQuery(id+"F16.opExtrude","SWEPT_FACE",FACE,{"disambiguationData":[OSD([sQuery(id+"F15.wireOp",EDGE,"72493947-4794-4d5b-8e6e-f786664ce59e.3")])]})]});
            var sketch = newSketch(context, id + "F26", { "sketchPlane" : qUnion([Q0])});
            skLineSegment(sketch, "E136", {"start": v(0, 0) * mm, "end": v(0, 25) * mm});
            skPoint(sketch, "E136.endSnap0", {"position": v(0, 0) * mm});
            skLineSegment(sketch, "E137", {"start": v(0, 25) * mm, "end": v(13, 25) * mm});
            skCircle(sketch, "E138", {"center": v(13, 25) * mm, "radius": 1.5 * mm});
            skLineSegment(sketch, "E139.MirrorCS", {"start": v(0, 25) * mm, "end": v(-13, 25) * mm});
            skCircle(sketch, "E140.MirrorC", {"center": v(-13, 25) * mm, "radius": 1.5 * mm});
            skSolve(sketch);
        }
        {
            var Q0;
            Q0=makeQuery(id+"F16.boolean.opBoolean","MERGE",FACE,{"derivedFrom":[makeQuery(id+"F1.opExtrude","SWEPT_FACE",FACE,{"disambiguationData":[OSD([sQuery(id+"F0.wireOp",EDGE,"E7.MirrorCS")])]}),makeQuery(id+"F16.opExtrude","SWEPT_FACE",FACE,{"disambiguationData":[OSD([sQuery(id+"F15.wireOp",EDGE,"72493947-4794-4d5b-8e6e-f786664ce59e.6")])]})]});
            var sketch = newSketch(context, id + "F27", { "sketchPlane" : qUnion([Q0])});
            skPoint(sketch, "E141.endSnap0", {"position": v(0, 0) * mm});
            skLineSegment(sketch, "E142", {"start": v(0, 39.9) * mm, "end": v(0, 33.9) * mm});
            skPoint(sketch, "E142.endSnap0", {"position": v(0, 39.9) * mm});
            skLineSegment(sketch, "E143", {"start": v(0, 33.9) * mm, "end": v(9, 33.9) * mm});
            skCircle(sketch, "E144", {"center": v(9, 33.9) * mm, "radius": 1.18 * mm});
            skCircle(sketch, "E145.MirrorC", {"center": v(-9, 33.9) * mm, "radius": 1.18 * mm});
            skArc(sketch, "E146", {"start": v(0, 33.9) * mm, "mid": v(5.4, 35.54) * mm, "end": v(9, 39.9) * mm});
            skArc(sketch, "E147.MirrorCS", {"start": v(0, 33.9) * mm, "mid": v(-5.4, 35.54) * mm, "end": v(-9, 39.9) * mm});
            skLineSegment(sketch, "E148", {"start": v(-9, 39.9) * mm, "end": v(9, 39.9) * mm});
            skSolve(sketch);
        }
        {
            var Q0;
            Q0 = qSketchRegion(id + "F27", true);
            var Q1;
            {var subQ0=sQuery(id+"F0.wireOp",EDGE,"E16.MirrorCS");Q1=makeQuery(id+"F16.boolean.opBoolean","MERGE",FACE,{"derivedFrom":[makeQuery(id+"F1.opExtrude","SWEPT_FACE",FACE,{"disambiguationData":[OSD([subQ0])]}),makeQuery(id+"F16.opExtrude","SWEPT_FACE",FACE,{"disambiguationData":[OSD([subQ0])]})]});}
            extrude(context, id + "F28", {"entities" : qUnion([Q0]), "operationType" : NewBodyOperationType.REMOVE, "endBound" : BoundingType.UP_TO_SURFACE, "oppositeDirection" : true, "endBoundEntityFace" : qUnion([Q1]), "depth" : 6.5 * mm});
        }
        {
            var Q0;
            Q0=makeQuery(id+"F1.opExtrude","CAP_FACE",FACE,{"disambiguationData":[OSD([sQuery(id+"F0.wireOp",EDGE,"E1"),sQuery(id+"F0.wireOp",EDGE,"E5"),sQuery(id+"F0.wireOp",EDGE,"E6"),sQuery(id+"F0.wireOp",EDGE,"E7.MirrorCS"),sQuery(id+"F0.wireOp",EDGE,"E15.MirrorCS"),sQuery(id+"F0.wireOp",EDGE,"E16.MirrorCS"),sQuery(id+"F0.wireOp",EDGE,"E18.MirrorCS"),sQuery(id+"F0.wireOp",EDGE,"E19")])],"isStart":false});
            var sketch = newSketch(context, id + "F29", { "sketchPlane" : qUnion([Q0])});
            skLineSegment(sketch, "E149", {"start": v(0, 0) * mm, "end": v(28.93, 28.93) * mm});
            skLineSegment(sketch, "E150", {"start": v(28.93, 28.93) * mm, "end": v(16.9, 40.95) * mm});
            skLineSegment(sketch, "E151", {"start": v(16.9, 40.95) * mm, "end": v(-40.95, -16.9) * mm});
            skLineSegment(sketch, "E152", {"start": v(-40.95, -16.9) * mm, "end": v(-16.9, -40.95) * mm});
            skLineSegment(sketch, "E153", {"start": v(-16.9, -40.95) * mm, "end": v(40.95, 16.9) * mm});
            skLineSegment(sketch, "E154", {"start": v(40.95, 16.9) * mm, "end": v(28.93, 28.93) * mm});
            skSolve(sketch);
        }
        {
            var Q0;
            Q0=makeQuery(id+"F29.imprint","IMPRINT",FACE,{"disambiguationData":[TD([[makeQuery(id+"F29.imprint","IMPRINT",EDGE,{"derivedFrom":sQuery(id+"F29.wireOp",EDGE,"078392c0-c6a0-4705-84cd-f0d4ae93a00a")}),-1.0]])]});
            var Q1;
            Q1=makeQuery(id+"F29.imprint","IMPRINT",FACE,{"disambiguationData":[TD([[makeQuery(id+"F29.imprint","IMPRINT",EDGE,{"derivedFrom":sQuery(id+"F29.wireOp",EDGE,"f5c87e50-7c17-449a-981f-098fc21e7771")}),-1.0]])]});
            var Q2;
            Q2=makeQuery(id+"F29.imprint","IMPRINT",FACE,{"disambiguationData":[TD([[makeQuery(id+"F29.imprint","IMPRINT",EDGE,{"derivedFrom":sQuery(id+"F29.wireOp",EDGE,"E150")}),-1.0]])]});
            var Q3;
            Q3=makeQuery(id+"F16.opExtrude","CAP_FACE",FACE,{"disambiguationData":[OSD([sQuery(id+"F0.wireOp",EDGE,"E1"),sQuery(id+"F0.wireOp",EDGE,"E5"),sQuery(id+"F0.wireOp",EDGE,"E6"),sQuery(id+"F0.wireOp",EDGE,"E7.MirrorCS"),sQuery(id+"F0.wireOp",EDGE,"E15.MirrorCS"),sQuery(id+"F0.wireOp",EDGE,"E16.MirrorCS"),sQuery(id+"F0.wireOp",EDGE,"E18.MirrorCS"),sQuery(id+"F0.wireOp",EDGE,"E19"),sQuery(id+"F10.wireOp",EDGE,"E76"),sQuery(id+"F10.wireOp",EDGE,"E78.MirrorC"),sQuery(id+"F10.wireOp",EDGE,"E80.MirrorC"),sQuery(id+"F10.wireOp",EDGE,"E82.MirrorC"),sQuery(id+"F15.wireOp",EDGE,"E102"),sQuery(id+"F15.wireOp",EDGE,"E104"),sQuery(id+"F15.wireOp",EDGE,"E110"),sQuery(id+"F15.wireOp",EDGE,"E112"),sQuery(id+"F15.wireOp",EDGE,"E114.0"),sQuery(id+"F15.wireOp",EDGE,"E114.1"),sQuery(id+"F15.wireOp",EDGE,"E114.2"),sQuery(id+"F15.wireOp",EDGE,"E114.3"),sQuery(id+"F15.wireOp",EDGE,"E114.4"),sQuery(id+"F15.wireOp",EDGE,"E114.5"),sQuery(id+"F15.wireOp",EDGE,"E114.6"),sQuery(id+"F15.wireOp",EDGE,"E114.7")])],"isStart":false});
            extrude(context, id + "F30", {"entities" : qUnion([Q0, Q1, Q2]), "operationType" : NewBodyOperationType.ADD, "endBound" : BoundingType.UP_TO_SURFACE, "endBoundEntityFace" : qUnion([Q3]), "depth" : 16 * mm});
        }
        {
            var Q0;
            Q0=makeQuery(id+"F30.boolean.opBoolean","SPLIT",FACE,{"disambiguationData":[TD([makeQuery(id+"F16.opExtrude","SWEPT_FACE",FACE,{"disambiguationData":[OSD([sQuery(id+"F15.wireOp",EDGE,"E114.0")])]})])],"derivedFrom":makeQuery(id+"F1.opExtrude","CAP_FACE",FACE,{"disambiguationData":[OSD([sQuery(id+"F0.wireOp",EDGE,"E1"),sQuery(id+"F0.wireOp",EDGE,"E5"),sQuery(id+"F0.wireOp",EDGE,"E6"),sQuery(id+"F0.wireOp",EDGE,"E7.MirrorCS"),sQuery(id+"F0.wireOp",EDGE,"E15.MirrorCS"),sQuery(id+"F0.wireOp",EDGE,"E16.MirrorCS"),sQuery(id+"F0.wireOp",EDGE,"E18.MirrorCS"),sQuery(id+"F0.wireOp",EDGE,"E19")])],"isStart":false})});
            var sketch = newSketch(context, id + "F31", { "sketchPlane" : qUnion([Q0])});
            skLineSegment(sketch, "E155", {"start": v(0, 0) * mm, "end": v(0, 21.57) * mm});
            skLineSegment(sketch, "E156", {"start": v(0, 0) * mm, "end": v(15.25, 15.25) * mm});
            skCircle(sketch, "E157", {"center": v(15.25, 15.25) * mm, "radius": 1.18 * mm});
            skLineSegment(sketch, "E158.MirrorCS", {"start": v(0, 0) * mm, "end": v(-15.25, 15.25) * mm});
            skCircle(sketch, "E159.MirrorC", {"center": v(-15.25, 15.25) * mm, "radius": 1.18 * mm});
            skCircle(sketch, "E160.MirrorC", {"center": v(-15.25, -15.25) * mm, "radius": 1.18 * mm});
            skCircle(sketch, "E161.MirrorC", {"center": v(15.25, -15.25) * mm, "radius": 1.18 * mm});
            skLineSegment(sketch, "E162.MirrorCS", {"start": v(0, 0) * mm, "end": v(-15.25, -15.25) * mm});
            skLineSegment(sketch, "E163.MirrorCS", {"start": v(0, 0) * mm, "end": v(15.25, -15.25) * mm});
            skCircle(sketch, "E164", {"center": v(0, 21.57) * mm, "radius": 1.18 * mm});
            skCircle(sketch, "E165.MirrorC", {"center": v(-21.57, 0) * mm, "radius": 1.18 * mm});
            skCircle(sketch, "E166.MirrorC", {"center": v(0, -21.57) * mm, "radius": 1.18 * mm});
            skLineSegment(sketch, "E167.MirrorCS", {"start": v(0, 0) * mm, "end": v(21.57, 0) * mm});
            skCircle(sketch, "E168.MirrorC", {"center": v(21.57, 0) * mm, "radius": 1.18 * mm});
            skLineSegment(sketch, "E169", {"start": v(15.25, 0) * mm, "end": v(15.25, 0) * mm});
            skLineSegment(sketch, "E170.MirrorCS", {"start": v(-15.25, 0) * mm, "end": v(-15.25, 0) * mm});
            skPoint(sketch, "E171.orphan", {"position": v(-15.25, 30.5) * mm});
            skPoint(sketch, "E172.trimOffspring.end.orphan", {"position": v(15.25, 30.5) * mm});
            skLineSegment(sketch, "E173", {"start": v(21.57, 0) * mm, "end": v(10.78, -10.78) * mm});
            skLineSegment(sketch, "E174", {"start": v(10.78, -10.78) * mm, "end": v(32.35, 10.78) * mm});
            skCircle(sketch, "E175", {"center": v(10.78, -10.78) * mm, "radius": 1.18 * mm});
            skCircle(sketch, "E176", {"center": v(32.35, 10.78) * mm, "radius": 1.18 * mm});
            skCircle(sketch, "E177.MirrorC", {"center": v(10.78, 32.35) * mm, "radius": 1.18 * mm});
            skCircle(sketch, "E178.MirrorC", {"center": v(-10.78, 10.78) * mm, "radius": 1.18 * mm});
            skCircle(sketch, "E179.MirrorC", {"center": v(-32.35, -10.78) * mm, "radius": 1.18 * mm});
            skCircle(sketch, "E180.MirrorC", {"center": v(-10.78, -32.35) * mm, "radius": 1.18 * mm});
            skSolve(sketch);
        }
        {
            var Q0;
            Q0=makeQuery(id+"F31.imprint","IMPRINT",FACE,{"disambiguationData":[TD([[makeQuery(id+"F31.imprint","IMPRINT",EDGE,{"derivedFrom":sQuery(id+"F31.wireOp",EDGE,"E157")}),1.0]])]});
            var Q1;
            Q1=makeQuery(id+"F31.imprint","IMPRINT",FACE,{"disambiguationData":[TD([[makeQuery(id+"F31.imprint","IMPRINT",EDGE,{"derivedFrom":sQuery(id+"F31.wireOp",EDGE,"E160.MirrorC")}),1.0]])]});
            var Q2;
            Q2=makeQuery(id+"F31.imprint","IMPRINT",FACE,{"disambiguationData":[TD([[makeQuery(id+"F31.imprint","IMPRINT",EDGE,{"derivedFrom":sQuery(id+"F31.wireOp",EDGE,"E164")}),1.0]])]});
            var Q3;
            Q3=makeQuery(id+"F31.imprint","IMPRINT",FACE,{"disambiguationData":[TD([[makeQuery(id+"F31.imprint","IMPRINT",EDGE,{"derivedFrom":sQuery(id+"F31.wireOp",EDGE,"E165.MirrorC")}),-1.0]])]});
            var Q4;
            Q4=makeQuery(id+"F31.imprint","IMPRINT",FACE,{"disambiguationData":[TD([[makeQuery(id+"F31.imprint","IMPRINT",EDGE,{"derivedFrom":sQuery(id+"F31.wireOp",EDGE,"E166.MirrorC")}),1.0]])]});
            var Q5;
            Q5=makeQuery(id+"F31.imprint","IMPRINT",FACE,{"disambiguationData":[TD([[makeQuery(id+"F31.imprint","IMPRINT",EDGE,{"derivedFrom":sQuery(id+"F31.wireOp",EDGE,"E176")}),1.0]])]});
            var Q6;
            Q6=makeQuery(id+"F31.imprint","IMPRINT",FACE,{"disambiguationData":[TD([[makeQuery(id+"F31.imprint","IMPRINT",EDGE,{"derivedFrom":sQuery(id+"F31.wireOp",EDGE,"E177.MirrorC")}),-1.0]])]});
            var Q7;
            Q7=makeQuery(id+"F31.imprint","IMPRINT",FACE,{"disambiguationData":[TD([[makeQuery(id+"F31.imprint","IMPRINT",EDGE,{"derivedFrom":sQuery(id+"F31.wireOp",EDGE,"E179.MirrorC")}),1.0]])]});
            var Q8;
            Q8=makeQuery(id+"F31.imprint","IMPRINT",FACE,{"disambiguationData":[TD([[makeQuery(id+"F31.imprint","IMPRINT",EDGE,{"derivedFrom":sQuery(id+"F31.wireOp",EDGE,"E180.MirrorC")}),-1.0]])]});
            var Q9;
            {var subQ0=sQuery(id+"F31.wireOp",EDGE,"E178.MirrorC");var subQ1=sQuery(id+"F31.wireOp",EDGE,"E158.MirrorCS");var subQ2=makeQuery(id+"F31.imprint","INTERSECT",VERTEX,{"disambiguationData":[OD(0.0)],"derivedFrom":[subQ1,subQ0]});Q9=makeQuery(id+"F31.imprint","IMPRINT",FACE,{"disambiguationData":[TD([[makeQuery(id+"F31.imprint","IMPRINT",EDGE,{"disambiguationData":[TD([[subQ2,1.0]])],"derivedFrom":subQ1}),1.0]])]});}
            var Q10;
            {var subQ0=sQuery(id+"F31.wireOp",EDGE,"E178.MirrorC");var subQ1=sQuery(id+"F31.wireOp",EDGE,"E158.MirrorCS");var subQ2=makeQuery(id+"F31.imprint","INTERSECT",VERTEX,{"disambiguationData":[OD(0.0)],"derivedFrom":[subQ1,subQ0]});Q10=makeQuery(id+"F31.imprint","IMPRINT",FACE,{"disambiguationData":[TD([[makeQuery(id+"F31.imprint","IMPRINT",EDGE,{"disambiguationData":[TD([[subQ2,1.0]])],"derivedFrom":subQ1}),-1.0]])]});}
            var Q11;
            Q11=makeQuery(id+"F31.imprint","IMPRINT",FACE,{"disambiguationData":[TD([[makeQuery(id+"F31.imprint","IMPRINT",EDGE,{"derivedFrom":sQuery(id+"F31.wireOp",EDGE,"E161.MirrorC")}),1.0]])]});
            var Q12;
            Q12=makeQuery(id+"F31.imprint","IMPRINT",FACE,{"disambiguationData":[TD([[makeQuery(id+"F31.imprint","IMPRINT",EDGE,{"derivedFrom":sQuery(id+"F31.wireOp",EDGE,"E159.MirrorC")}),-1.0]])]});
            var Q13;
            {var subQ0=sQuery(id+"F31.wireOp",EDGE,"E174");var subQ1=sQuery(id+"F31.wireOp",EDGE,"E167.MirrorCS");var subQ2=makeQuery(id+"F31.imprint","INTERSECT",VERTEX,{"derivedFrom":[subQ1,subQ0]});Q13=makeQuery(id+"F31.imprint","IMPRINT",FACE,{"disambiguationData":[TD([[makeQuery(id+"F31.imprint","IMPRINT",EDGE,{"disambiguationData":[TD([[subQ2,1.0]])],"derivedFrom":subQ1}),1.0]])]});}
            var Q14;
            {var subQ0=sQuery(id+"F31.wireOp",EDGE,"E163.MirrorCS");var subQ1=makeQuery(id+"F31.imprint","INTERSECT",VERTEX,{"derivedFrom":[subQ0,sQuery(id+"F31.wireOp",EDGE,"E174")]});Q14=makeQuery(id+"F31.imprint","IMPRINT",FACE,{"disambiguationData":[TD([[makeQuery(id+"F31.imprint","IMPRINT",EDGE,{"disambiguationData":[TD([[subQ1,1.0]])],"derivedFrom":subQ0}),-1.0]])]});}
            var Q15;
            {var subQ0=sQuery(id+"F31.wireOp",EDGE,"E174");var subQ1=sQuery(id+"F31.wireOp",EDGE,"E163.MirrorCS");var subQ2=makeQuery(id+"F31.imprint","INTERSECT",VERTEX,{"derivedFrom":[subQ1,subQ0]});Q15=makeQuery(id+"F31.imprint","IMPRINT",FACE,{"disambiguationData":[TD([[makeQuery(id+"F31.imprint","IMPRINT",EDGE,{"disambiguationData":[TD([[subQ2,-1.0]])],"derivedFrom":subQ1}),1.0]])]});}
            var Q16;
            {var subQ0=sQuery(id+"F31.wireOp",EDGE,"E174");var subQ1=sQuery(id+"F31.wireOp",EDGE,"E168.MirrorC");var subQ2=makeQuery(id+"F31.imprint","INTERSECT",VERTEX,{"disambiguationData":[OD(0.0)],"derivedFrom":[subQ1,subQ0]});Q16=makeQuery(id+"F31.imprint","IMPRINT",FACE,{"disambiguationData":[TD([[makeQuery(id+"F31.imprint","IMPRINT",EDGE,{"disambiguationData":[TD([[subQ2,-1.0]])],"derivedFrom":subQ1}),-1.0]])]});}
            var Q17;
            {var subQ0=sQuery(id+"F31.wireOp",EDGE,"E174");var subQ1=sQuery(id+"F31.wireOp",EDGE,"E167.MirrorCS");var subQ2=makeQuery(id+"F31.imprint","INTERSECT",VERTEX,{"derivedFrom":[subQ1,subQ0]});Q17=makeQuery(id+"F31.imprint","IMPRINT",FACE,{"disambiguationData":[TD([[makeQuery(id+"F31.imprint","IMPRINT",EDGE,{"disambiguationData":[TD([[subQ2,1.0]])],"derivedFrom":subQ1}),-1.0]])]});}
            var Q18;
            {var subQ0=sQuery(id+"F31.wireOp",EDGE,"E174");var subQ1=sQuery(id+"F31.wireOp",EDGE,"E163.MirrorCS");var subQ2=makeQuery(id+"F31.imprint","INTERSECT",VERTEX,{"derivedFrom":[subQ1,subQ0]});Q18=makeQuery(id+"F31.imprint","IMPRINT",FACE,{"disambiguationData":[TD([[makeQuery(id+"F31.imprint","IMPRINT",EDGE,{"disambiguationData":[TD([[subQ2,1.0]])],"derivedFrom":subQ1}),1.0]])]});}
            var Q19;
            Q19=makeQuery(id+"F30.boolean.opBoolean","MERGE",FACE,{"derivedFrom":[makeQuery(id+"F16.opExtrude","CAP_FACE",FACE,{"disambiguationData":[OSD([sQuery(id+"F0.wireOp",EDGE,"E1"),sQuery(id+"F0.wireOp",EDGE,"E5"),sQuery(id+"F0.wireOp",EDGE,"E6"),sQuery(id+"F0.wireOp",EDGE,"E7.MirrorCS"),sQuery(id+"F0.wireOp",EDGE,"E15.MirrorCS"),sQuery(id+"F0.wireOp",EDGE,"E16.MirrorCS"),sQuery(id+"F0.wireOp",EDGE,"E18.MirrorCS"),sQuery(id+"F0.wireOp",EDGE,"E19"),sQuery(id+"F10.wireOp",EDGE,"E76"),sQuery(id+"F10.wireOp",EDGE,"E78.MirrorC"),sQuery(id+"F10.wireOp",EDGE,"E80.MirrorC"),sQuery(id+"F10.wireOp",EDGE,"E82.MirrorC"),sQuery(id+"F15.wireOp",EDGE,"E102"),sQuery(id+"F15.wireOp",EDGE,"E104"),sQuery(id+"F15.wireOp",EDGE,"E110"),sQuery(id+"F15.wireOp",EDGE,"E112"),sQuery(id+"F15.wireOp",EDGE,"E114.0"),sQuery(id+"F15.wireOp",EDGE,"E114.1"),sQuery(id+"F15.wireOp",EDGE,"E114.2"),sQuery(id+"F15.wireOp",EDGE,"E114.3"),sQuery(id+"F15.wireOp",EDGE,"E114.4"),sQuery(id+"F15.wireOp",EDGE,"E114.5"),sQuery(id+"F15.wireOp",EDGE,"E114.6"),sQuery(id+"F15.wireOp",EDGE,"E114.7")])],"isStart":false}),makeQuery(id+"F30.opExtrude","CAP_FACE",FACE,{"disambiguationData":[OSD([sQuery(id+"F29.wireOp",EDGE,"E150"),sQuery(id+"F29.wireOp",EDGE,"E151"),sQuery(id+"F29.wireOp",EDGE,"E152"),sQuery(id+"F29.wireOp",EDGE,"E153"),sQuery(id+"F29.wireOp",EDGE,"E154")])],"isStart":false})]});
            extrude(context, id + "F32", {"entities" : qUnion([Q0, Q1, Q2, Q3, Q4, Q5, Q6, Q7, Q8, Q9, Q10, Q11, Q12, Q13, Q14, Q15, Q16, Q17, Q18]), "operationType" : NewBodyOperationType.REMOVE, "endBound" : BoundingType.UP_TO_SURFACE, "endBoundEntityFace" : qUnion([Q19]), "depth" : 25 * mm});
        }
        {
            var Q0;
            Q0=makeQuery(id+"F25.imprint","IMPRINT",FACE,{"disambiguationData":[TD([[makeQuery(id+"F25.imprint","IMPRINT",EDGE,{"derivedFrom":sQuery(id+"F25.wireOp",EDGE,"E133")}),-1.0]])]});
            var sketch = newSketch(context, id + "F33", { "sketchPlane" : qUnion([Q0])});
            skLineSegment(sketch, "E181", {"start": v(0, 0) * mm, "end": v(0, 2) * mm});
            skLineSegment(sketch, "E182", {"start": v(0, 2) * mm, "end": v(11.9, 2) * mm});
            skLineSegment(sketch, "E183", {"start": v(13.9, 4) * mm, "end": v(13.9, 35.9) * mm});
            skLineSegment(sketch, "E184", {"start": v(11.9, 37.9) * mm, "end": v(0, 37.9) * mm});
            skPoint(sketch, "E185.visualSharp", {"position": v(13.9, 2) * mm});
            skArc(sketch, "E185.filletArc", {"start": v(11.9, 2) * mm, "mid": v(13.31, 2.59) * mm, "end": v(13.9, 4) * mm});
            skPoint(sketch, "E186.visualSharp", {"position": v(13.9, 37.9) * mm});
            skArc(sketch, "E186.filletArc", {"start": v(13.9, 35.9) * mm, "mid": v(13.31, 37.31) * mm, "end": v(11.9, 37.9) * mm});
            skLineSegment(sketch, "E187.MirrorCS", {"start": v(-11.9, 37.9) * mm, "end": v(0, 37.9) * mm});
            skLineSegment(sketch, "E188.MirrorCS", {"start": v(0, 2) * mm, "end": v(-11.9, 2) * mm});
            skArc(sketch, "E189.MirrorCS", {"start": v(-13.9, 35.9) * mm, "mid": v(-13.31, 37.31) * mm, "end": v(-11.9, 37.9) * mm});
            skPoint(sketch, "E190.MirrorP", {"position": v(-13.9, 37.9) * mm});
            skArc(sketch, "E191.MirrorCS", {"start": v(-11.9, 2) * mm, "mid": v(-13.31, 2.59) * mm, "end": v(-13.9, 4) * mm});
            skPoint(sketch, "E192.MirrorP", {"position": v(-13.9, 2) * mm});
            skLineSegment(sketch, "E193.MirrorCS", {"start": v(-13.9, 4) * mm, "end": v(-13.9, 35.9) * mm});
            skSolve(sketch);
        }
        {
            var Q0;
            Q0 = qSketchRegion(id + "F33", true);
            extrude(context, id + "F34", {"entities" : qUnion([Q0]), "operationType" : NewBodyOperationType.REMOVE, "endBound" : BoundingType.THROUGH_ALL, "oppositeDirection" : true, "depth" : 25 * mm});
        }
        {
            var Q0;
            Q0=makeQuery(id+"F30.boolean.opBoolean","SPLIT",FACE,{"disambiguationData":[TD([makeQuery(id+"F16.opExtrude","SWEPT_FACE",FACE,{"disambiguationData":[OSD([sQuery(id+"F15.wireOp",EDGE,"E114.0")])]})])],"derivedFrom":makeQuery(id+"F1.opExtrude","CAP_FACE",FACE,{"disambiguationData":[OSD([sQuery(id+"F0.wireOp",EDGE,"E1"),sQuery(id+"F0.wireOp",EDGE,"E5"),sQuery(id+"F0.wireOp",EDGE,"E6"),sQuery(id+"F0.wireOp",EDGE,"E7.MirrorCS"),sQuery(id+"F0.wireOp",EDGE,"E15.MirrorCS"),sQuery(id+"F0.wireOp",EDGE,"E16.MirrorCS"),sQuery(id+"F0.wireOp",EDGE,"E18.MirrorCS"),sQuery(id+"F0.wireOp",EDGE,"E19")])],"isStart":false})});
            var sketch = newSketch(context, id + "F35", { "sketchPlane" : qUnion([Q0])});
            skLineSegment(sketch, "E194", {"start": v(-28.93, 28.93) * mm, "end": v(-20.02, 20.02) * mm});
            skLineSegment(sketch, "E195", {"start": v(-20.02, 20.02) * mm, "end": v(-12, 12) * mm});
            skLineSegment(sketch, "E196", {"start": v(-12, 12) * mm, "end": v(-4.51, 19.5) * mm});
            skArc(sketch, "E197", {"start": v(-11.1, 28.93) * mm, "mid": v(-28.93, 28.93) * mm, "end": v(-28.93, 11.1) * mm});
            skLineSegment(sketch, "E198", {"start": v(-12, 12) * mm, "end": v(-19.5, 4.51) * mm});
            skLineSegment(sketch, "E199", {"start": v(-22.33, 4.51) * mm, "end": v(-28.93, 11.1) * mm});
            skLineSegment(sketch, "E200", {"start": v(-4.51, 22.33) * mm, "end": v(-11.1, 28.93) * mm});
            skPoint(sketch, "E201.visualSharp", {"position": v(-3.1, 20.92) * mm});
            skArc(sketch, "E201.filletArc", {"start": v(-4.51, 19.5) * mm, "mid": v(-3.93, 20.92) * mm, "end": v(-4.51, 22.33) * mm});
            skPoint(sketch, "E202.visualSharp", {"position": v(-20.92, 3.1) * mm});
            skArc(sketch, "E202.filletArc", {"start": v(-22.33, 4.51) * mm, "mid": v(-20.92, 3.93) * mm, "end": v(-19.5, 4.51) * mm});
            skLineSegment(sketch, "E203", {"start": v(0, 0) * mm, "end": v(7.19, 7.19) * mm});
            skLineSegment(sketch, "E204", {"start": v(-28.93, 28.93) * mm, "end": v(-28.93, 28.93) * mm});
            skPoint(sketch, "E204.endSnap0", {"position": v(-28.93, 28.93) * mm});
            skArc(sketch, "E205.MirrorCS", {"start": v(19.5, -4.51) * mm, "mid": v(20.92, -3.93) * mm, "end": v(22.33, -4.51) * mm});
            skArc(sketch, "E206.MirrorCS", {"start": v(4.51, -22.33) * mm, "mid": v(3.93, -20.92) * mm, "end": v(4.51, -19.5) * mm});
            skPoint(sketch, "E207.MirrorP", {"position": v(28.93, -28.93) * mm});
            skPoint(sketch, "E208.MirrorP", {"position": v(20.92, -3.1) * mm});
            skLineSegment(sketch, "E209.MirrorCS", {"start": v(20.02, -20.02) * mm, "end": v(12, -12) * mm});
            skLineSegment(sketch, "E210.MirrorCS", {"start": v(12, -12) * mm, "end": v(19.5, -4.51) * mm});
            skArc(sketch, "E211.MirrorCS", {"start": v(28.93, -11.1) * mm, "mid": v(28.93, -28.93) * mm, "end": v(11.1, -28.93) * mm});
            skLineSegment(sketch, "E212.MirrorCS", {"start": v(28.93, -28.93) * mm, "end": v(20.02, -20.02) * mm});
            skLineSegment(sketch, "E213.MirrorCS", {"start": v(28.93, -28.93) * mm, "end": v(28.93, -28.93) * mm});
            skLineSegment(sketch, "E214.MirrorCS", {"start": v(22.33, -4.51) * mm, "end": v(28.93, -11.1) * mm});
            skLineSegment(sketch, "E215.MirrorCS", {"start": v(12, -12) * mm, "end": v(4.51, -19.5) * mm});
            skPoint(sketch, "E216.MirrorP", {"position": v(3.1, -20.92) * mm});
            skLineSegment(sketch, "E217.MirrorCS", {"start": v(4.51, -22.33) * mm, "end": v(11.1, -28.93) * mm});
            skSolve(sketch);
        }
        {
            var Q0;
            Q0 = qSketchRegion(id + "F35", true);
            var Q1;
            Q1=makeQuery(id+"F1.opExtrude","CAP_FACE",FACE,{"disambiguationData":[OSD([sQuery(id+"F0.wireOp",EDGE,"E1"),sQuery(id+"F0.wireOp",EDGE,"E5"),sQuery(id+"F0.wireOp",EDGE,"E6"),sQuery(id+"F0.wireOp",EDGE,"E7.MirrorCS"),sQuery(id+"F0.wireOp",EDGE,"E15.MirrorCS"),sQuery(id+"F0.wireOp",EDGE,"E16.MirrorCS"),sQuery(id+"F0.wireOp",EDGE,"E18.MirrorCS"),sQuery(id+"F0.wireOp",EDGE,"E19")])],"isStart":true});
            extrude(context, id + "F36", {"entities" : qUnion([Q0]), "operationType" : NewBodyOperationType.REMOVE, "endBound" : BoundingType.UP_TO_SURFACE, "oppositeDirection" : true, "endBoundEntityFace" : qUnion([Q1]), "depth" : 26 * mm});
        }
        {
            var Q0;
            Q0=makeQuery(id+"F1.opExtrude","CAP_FACE",FACE,{"disambiguationData":[OSD([sQuery(id+"F0.wireOp",EDGE,"E1"),sQuery(id+"F0.wireOp",EDGE,"E5"),sQuery(id+"F0.wireOp",EDGE,"E6"),sQuery(id+"F0.wireOp",EDGE,"E7.MirrorCS"),sQuery(id+"F0.wireOp",EDGE,"E15.MirrorCS"),sQuery(id+"F0.wireOp",EDGE,"E16.MirrorCS"),sQuery(id+"F0.wireOp",EDGE,"E18.MirrorCS"),sQuery(id+"F0.wireOp",EDGE,"E19")])],"isStart":true});
            var sketch = newSketch(context, id + "F37", { "sketchPlane" : qUnion([Q0])});
            skLineSegment(sketch, "E218", {"start": v(0, 0) * mm, "end": v(-15.25, 0) * mm});
            skLineSegment(sketch, "E219", {"start": v(-15.25, 0) * mm, "end": v(-15.25, 15.25) * mm});
            skCircle(sketch, "E220", {"center": v(-15.25, 15.25) * mm, "radius": 1.18 * mm});
            skLineSegment(sketch, "E221", {"start": v(0, 0) * mm, "end": v(15.25, 0) * mm});
            skLineSegment(sketch, "E222", {"start": v(15.25, 0) * mm, "end": v(15.25, -15.25) * mm});
            skCircle(sketch, "E223", {"center": v(15.25, -15.25) * mm, "radius": 1.18 * mm});
            skLineSegment(sketch, "E224", {"start": v(30.63, 30.63) * mm, "end": v(28.93, 28.93) * mm});
            skLineSegment(sketch, "E225", {"start": v(30.63, 30.63) * mm, "end": v(41.59, 19.66) * mm});
            skLineSegment(sketch, "E226", {"start": v(41.59, 19.66) * mm, "end": v(38.4, 16.48) * mm});
            skCircle(sketch, "E227", {"center": v(38.4, 16.48) * mm, "radius": 0.85 * mm});
            skLineSegment(sketch, "E228", {"start": v(0, 0) * mm, "end": v(15.25, -15.25) * mm});
            skLineSegment(sketch, "E229.MirrorCS", {"start": v(19.66, 41.58) * mm, "end": v(16.48, 38.4) * mm});
            skCircle(sketch, "E230.MirrorC", {"center": v(16.48, 38.4) * mm, "radius": 0.85 * mm});
            skLineSegment(sketch, "E231.MirrorCS", {"start": v(30.63, 30.63) * mm, "end": v(19.66, 41.58) * mm});
            skLineSegment(sketch, "E232.MirrorCS", {"start": v(-30.63, -30.63) * mm, "end": v(-28.93, -28.93) * mm});
            skCircle(sketch, "E233.MirrorC", {"center": v(-16.48, -38.4) * mm, "radius": 0.85 * mm});
            skCircle(sketch, "E234.MirrorC", {"center": v(-38.4, -16.48) * mm, "radius": 0.85 * mm});
            skLineSegment(sketch, "E235.MirrorCS", {"start": v(-41.58, -19.66) * mm, "end": v(-38.4, -16.48) * mm});
            skLineSegment(sketch, "E236.MirrorCS", {"start": v(-19.66, -41.59) * mm, "end": v(-16.48, -38.4) * mm});
            skLineSegment(sketch, "E237.MirrorCS", {"start": v(-30.62, -30.63) * mm, "end": v(-41.58, -19.66) * mm});
            skLineSegment(sketch, "E238.MirrorCS", {"start": v(-30.63, -30.63) * mm, "end": v(-19.66, -41.59) * mm});
            skSolve(sketch);
        }
        {
            var Q0;
            Q0=makeQuery(id+"F37.imprint","IMPRINT",FACE,{"disambiguationData":[TD([[makeQuery(id+"F37.imprint","IMPRINT",EDGE,{"derivedFrom":sQuery(id+"F37.wireOp",EDGE,"E220")}),1.0]])]});
            var Q1;
            Q1=makeQuery(id+"F37.imprint","IMPRINT",FACE,{"disambiguationData":[TD([[makeQuery(id+"F37.imprint","IMPRINT",EDGE,{"derivedFrom":sQuery(id+"F37.wireOp",EDGE,"E227")}),1.0]])]});
            var Q2;
            Q2=makeQuery(id+"F37.imprint","IMPRINT",FACE,{"disambiguationData":[TD([[makeQuery(id+"F37.imprint","IMPRINT",EDGE,{"derivedFrom":sQuery(id+"F37.wireOp",EDGE,"E230.MirrorC")}),-1.0]])]});
            var Q3;
            Q3=makeQuery(id+"F37.imprint","IMPRINT",FACE,{"disambiguationData":[TD([[makeQuery(id+"F37.imprint","IMPRINT",EDGE,{"derivedFrom":sQuery(id+"F37.wireOp",EDGE,"E233.MirrorC")}),-1.0]])]});
            var Q4;
            Q4=makeQuery(id+"F37.imprint","IMPRINT",FACE,{"disambiguationData":[TD([[makeQuery(id+"F37.imprint","IMPRINT",EDGE,{"derivedFrom":sQuery(id+"F37.wireOp",EDGE,"E234.MirrorC")}),1.0]])]});
            var Q5;
            {var subQ0=sQuery(id+"F37.wireOp",EDGE,"E228");var subQ1=sQuery(id+"F37.wireOp",EDGE,"E222");var subQ2=makeQuery(id+"F37.imprint","INTERSECT",VERTEX,{"derivedFrom":[subQ1,subQ0]});Q5=makeQuery(id+"F37.imprint","IMPRINT",FACE,{"disambiguationData":[TD([[makeQuery(id+"F37.imprint","IMPRINT",EDGE,{"disambiguationData":[TD([[subQ2,1.0]])],"derivedFrom":subQ1}),-1.0]])]});}
            var Q6;
            {var subQ0=sQuery(id+"F37.wireOp",EDGE,"E228");var subQ1=sQuery(id+"F37.wireOp",EDGE,"E222");var subQ2=makeQuery(id+"F37.imprint","INTERSECT",VERTEX,{"derivedFrom":[subQ1,subQ0]});Q6=makeQuery(id+"F37.imprint","IMPRINT",FACE,{"disambiguationData":[TD([[makeQuery(id+"F37.imprint","IMPRINT",EDGE,{"disambiguationData":[TD([[subQ2,1.0]])],"derivedFrom":subQ1}),1.0]])]});}
            extrude(context, id + "F38", {"entities" : qUnion([Q0, Q1, Q2, Q3, Q4, Q5, Q6]), "operationType" : NewBodyOperationType.REMOVE, "oppositeDirection" : true, "depth" : 5 * mm});
        }
        {
            var Q0;
            Q0=makeQuery(id+"F16.boolean.opBoolean","MERGE",FACE,{"derivedFrom":[makeQuery(id+"F1.opExtrude","SWEPT_FACE",FACE,{"disambiguationData":[OSD([sQuery(id+"F0.wireOp",EDGE,"E7.MirrorCS")])]}),makeQuery(id+"F16.opExtrude","SWEPT_FACE",FACE,{"disambiguationData":[OSD([sQuery(id+"F15.wireOp",EDGE,"E104")])]})]});
            var sketch = newSketch(context, id + "F39", { "sketchPlane" : qUnion([Q0])});
            skLineSegment(sketch, "E239", {"start": v(0, 0) * mm, "end": v(0, 4) * mm});
            skPoint(sketch, "E239.endSnap0", {"position": v(0, 0) * mm});
            skLineSegment(sketch, "E240", {"start": v(0, 4) * mm, "end": v(15.5, 4) * mm});
            skCircle(sketch, "E241", {"center": v(15.5, 4) * mm, "radius": 1.2 * mm});
            skCircle(sketch, "E242.MirrorC", {"center": v(-15.5, 4) * mm, "radius": 1.2 * mm});
            skSolve(sketch);
        }
        {
            var Q0;
            Q0 = qSketchRegion(id + "F39", true);
            extrude(context, id + "F40", {"entities" : qUnion([Q0]), "operationType" : NewBodyOperationType.REMOVE, "oppositeDirection" : true, "depth" : 5.25 * mm});
        }
        {
            var Q0;
            Q0=makeQuery(id+"F1.opExtrude","SWEPT_FACE",FACE,{"disambiguationData":[OSD([sQuery(id+"F0.wireOp",EDGE,"E16.MirrorCS")])]});
            var sketch = newSketch(context, id + "F41", { "sketchPlane" : qUnion([Q0])});
            skLineSegment(sketch, "E243", {"start": v(0, 0) * mm, "end": v(0, 4) * mm});
            skLineSegment(sketch, "E244", {"start": v(0, 4) * mm, "end": v(15.5, 4) * mm});
            skCircle(sketch, "E245", {"center": v(15.5, 4) * mm, "radius": 1.2 * mm});
            skCircle(sketch, "E246.MirrorC", {"center": v(-15.5, 4) * mm, "radius": 1.2 * mm});
            skSolve(sketch);
        }
        {
            var Q0;
            Q0 = qSketchRegion(id + "F41", true);
            extrude(context, id + "F42", {"entities" : qUnion([Q0]), "operationType" : NewBodyOperationType.REMOVE, "oppositeDirection" : true, "depth" : 5.25 * mm});
        }
    });
